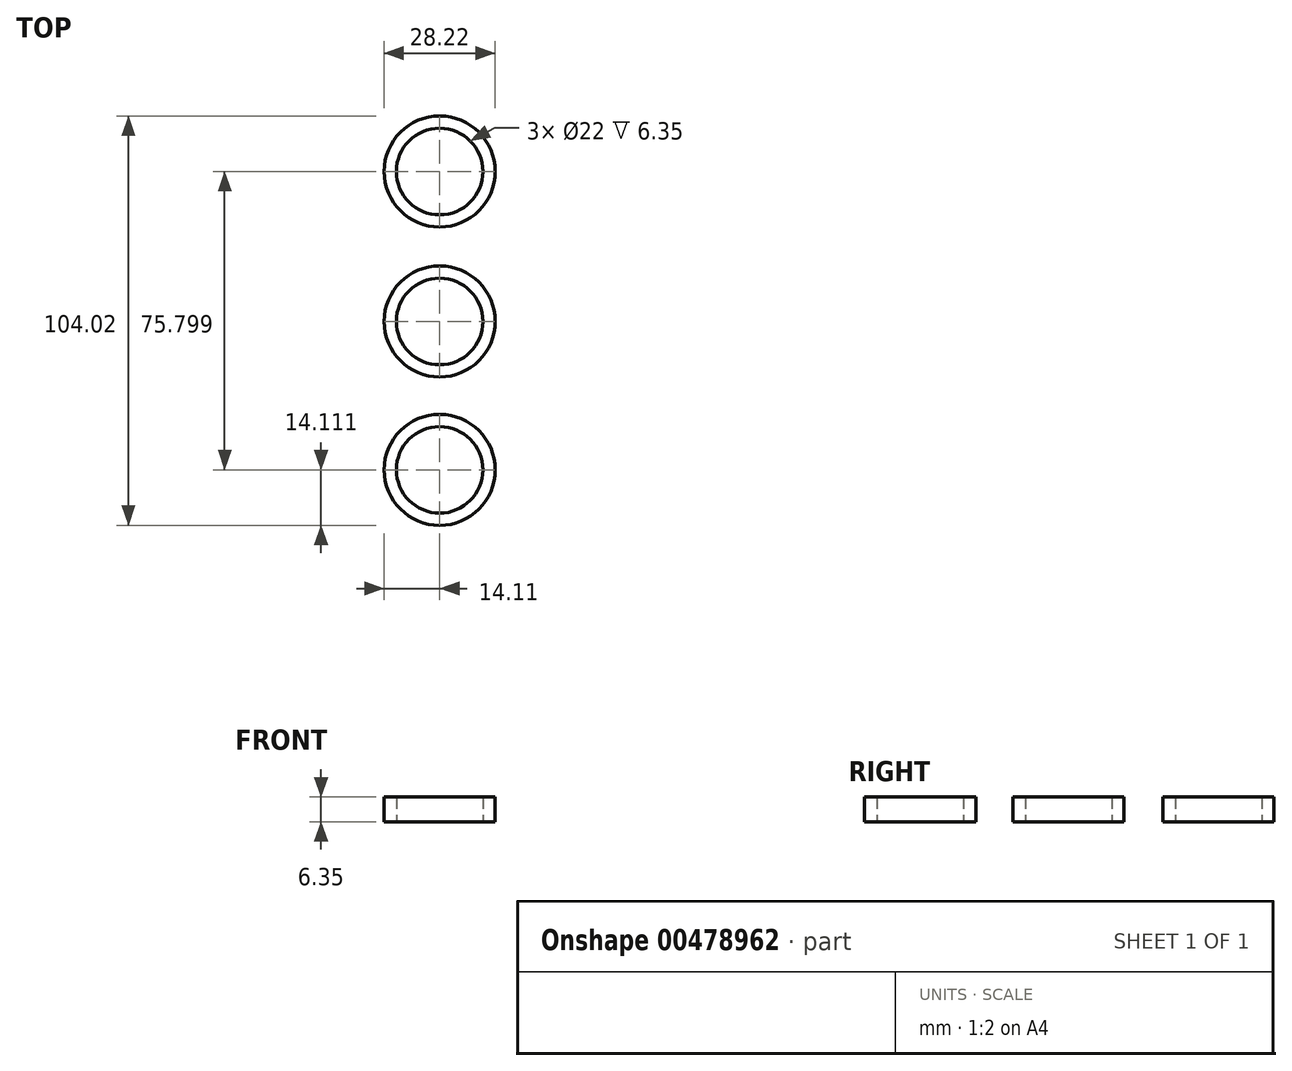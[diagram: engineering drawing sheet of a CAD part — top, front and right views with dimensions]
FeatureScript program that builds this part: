
annotation { "Feature Type Name" : "Feature", "Feature Type Description" : "" }
export const myFeature = defineFeature(function(context is Context, id is Id, definition is map)
    precondition{}
    {
        {
            var Q0;
            Q0=qCreatedBy(makeId("Top.planeOp"),FACE);
            var sketch = newSketch(context, id + "F0", { "sketchPlane" : qUnion([Q0])});
            skCircle(sketch, "E0", {"center": v(0, 0) * mm, "radius": 14.1 * mm});
            skCircle(sketch, "E1", {"center": v(0, 38.1) * mm, "radius": 14.1 * mm});
            skCircle(sketch, "E2", {"center": v(0, -37.7) * mm, "radius": 14.1 * mm});
            skCircle(sketch, "E3", {"center": v(0, 38.1) * mm, "radius": 11 * mm});
            skCircle(sketch, "E4", {"center": v(0, 0) * mm, "radius": 11 * mm});
            skCircle(sketch, "E5", {"center": v(0, -37.7) * mm, "radius": 11 * mm});
            skSolve(sketch);
        }
        {
            var Q0;
            Q0=makeQuery(id+"F0.imprint","IMPRINT",FACE,{"disambiguationData":[TD([[makeQuery(id+"F0.imprint","IMPRINT",EDGE,{"derivedFrom":sQuery(id+"F0.wireOp",EDGE,"E1")}),1.0]])]});
            var Q1;
            Q1=makeQuery(id+"F0.imprint","IMPRINT",FACE,{"disambiguationData":[TD([[makeQuery(id+"F0.imprint","IMPRINT",EDGE,{"derivedFrom":sQuery(id+"F0.wireOp",EDGE,"E2")}),1.0]])]});
            var Q2;
            Q2=makeQuery(id+"F0.imprint","IMPRINT",FACE,{"disambiguationData":[TD([[makeQuery(id+"F0.imprint","IMPRINT",EDGE,{"derivedFrom":sQuery(id+"F0.wireOp",EDGE,"E0")}),1.0]])]});
            extrude(context, id + "F1", {"entities" : qUnion([Q0, Q1, Q2]), "depth" : 6.35 * mm});
        }
    });
